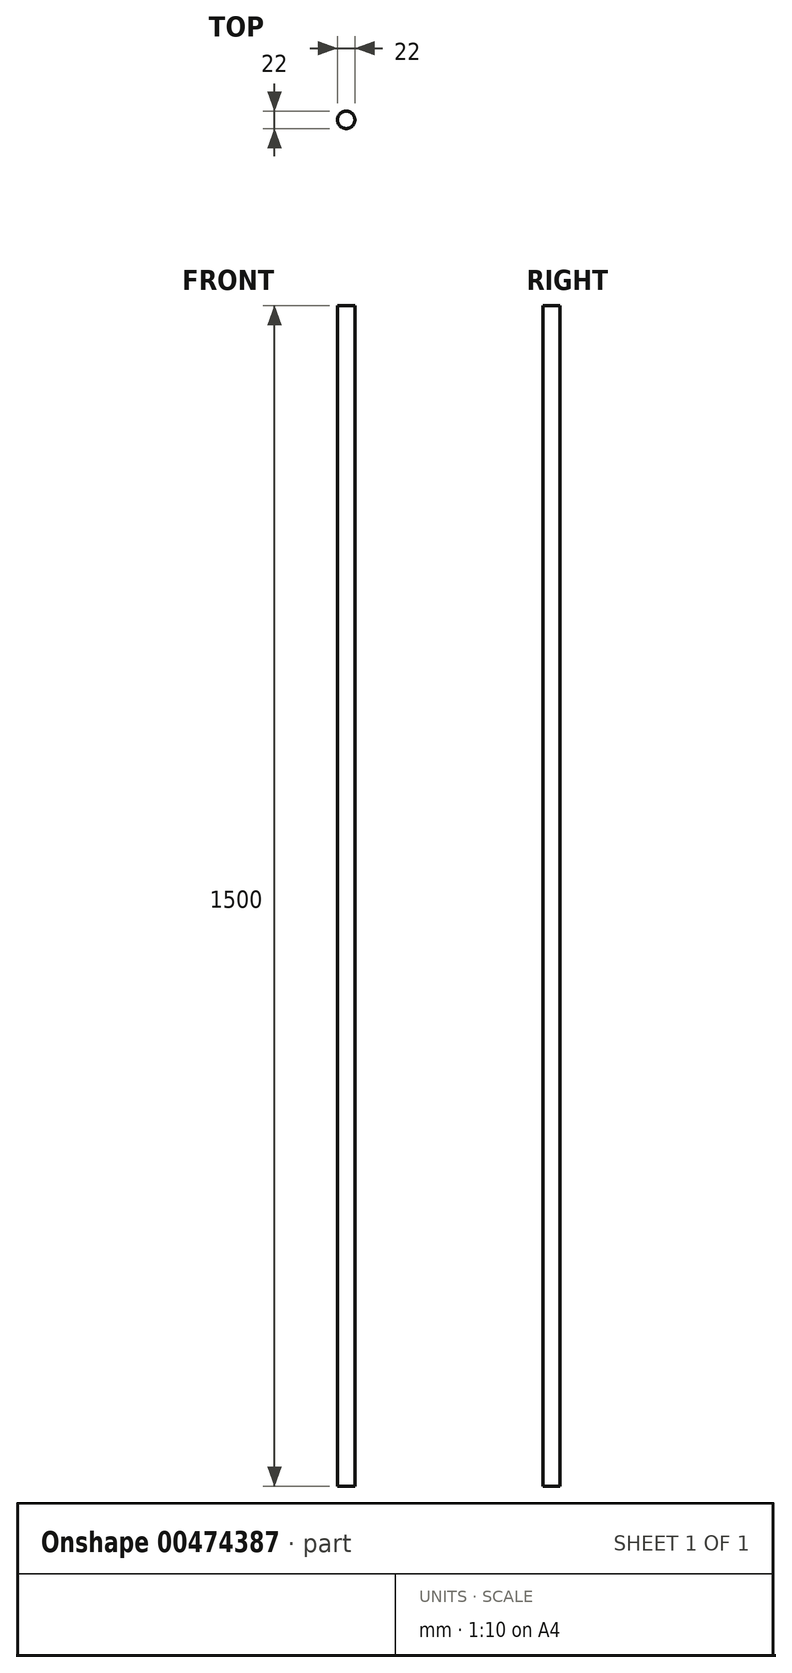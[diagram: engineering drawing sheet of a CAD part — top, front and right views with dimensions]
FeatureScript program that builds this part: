
annotation { "Feature Type Name" : "Feature", "Feature Type Description" : "" }
export const myFeature = defineFeature(function(context is Context, id is Id, definition is map)
    precondition{}
    {
        {
            var Q0;
            Q0=qCreatedBy(makeId("Top.planeOp"),FACE);
            var sketch = newSketch(context, id + "F0", { "sketchPlane" : qUnion([Q0])});
            skCircle(sketch, "E0", {"center": v(0, 0) * mm, "radius": 11 * mm});
            skSolve(sketch);
        }
        {
            var Q0;
            Q0 = qSketchRegion(id + "F0", true);
            extrude(context, id + "F1", {"entities" : qUnion([Q0]), "depth" : 1500 * mm});
        }
    });
